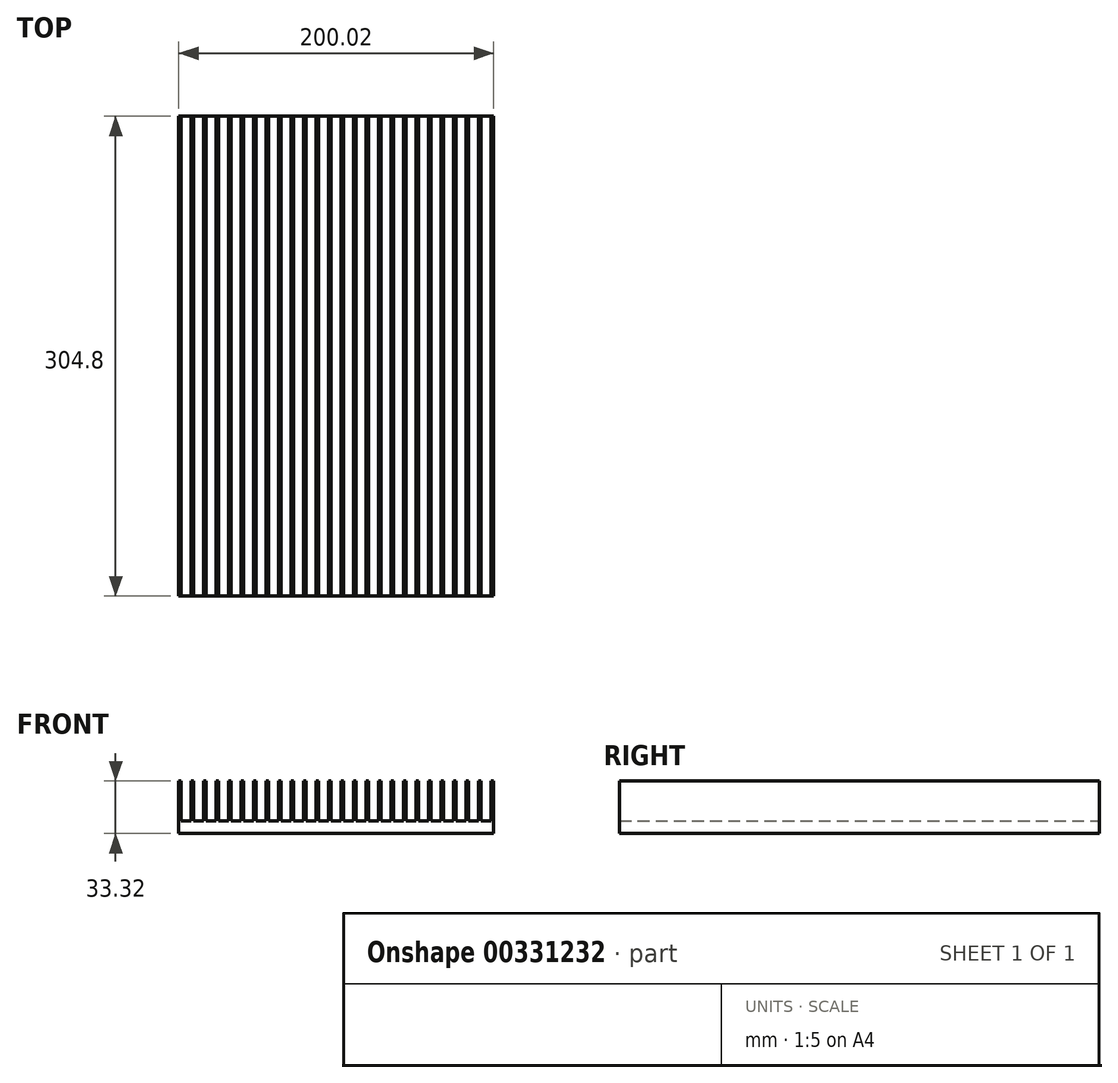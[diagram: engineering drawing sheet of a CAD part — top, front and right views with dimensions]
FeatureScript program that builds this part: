
annotation { "Feature Type Name" : "Feature", "Feature Type Description" : "" }
export const myFeature = defineFeature(function(context is Context, id is Id, definition is map)
    precondition{}
    {
        {
            var Q0;
            Q0=qCreatedBy(makeId("Front.planeOp"),FACE);
            var sketch = newSketch(context, id + "F0", { "sketchPlane" : qUnion([Q0])});
            skLineSegment(sketch, "E0", {"start": v(-100.01, 0) * mm, "end": v(100.01, 0) * mm});
            skLineSegment(sketch, "E1", {"start": v(-100.01, 0) * mm, "end": v(-100.01, 33.32) * mm});
            skLineSegment(sketch, "E2", {"start": v(-100.01, 33.32) * mm, "end": v(-98.49, 33.32) * mm});
            skLineSegment(sketch, "E3", {"start": v(-98.49, 33.32) * mm, "end": v(-98.49, 7.92) * mm});
            skLineSegment(sketch, "E4", {"start": v(-98.49, 7.92) * mm, "end": v(-92.07, 7.92) * mm});
            skLineSegment(sketch, "E5", {"start": v(-92.07, 7.92) * mm, "end": v(-92.07, 33.32) * mm});
            skLineSegment(sketch, "E6", {"start": v(-92.07, 33.32) * mm, "end": v(-90.55, 33.32) * mm});
            skLineSegment(sketch, "E7", {"start": v(-90.55, 33.32) * mm, "end": v(-90.55, 7.92) * mm});
            skLineSegment(sketch, "E8", {"start": v(-90.55, 7.92) * mm, "end": v(-84.13, 7.92) * mm});
            skLineSegment(sketch, "E9", {"start": v(-84.13, 7.92) * mm, "end": v(-84.13, 33.32) * mm});
            skLineSegment(sketch, "E10", {"start": v(-84.13, 33.32) * mm, "end": v(-82.6, 33.32) * mm});
            skLineSegment(sketch, "E11", {"start": v(-82.6, 33.32) * mm, "end": v(-82.6, 7.92) * mm});
            skLineSegment(sketch, "E12", {"start": v(-82.6, 7.92) * mm, "end": v(-76.2, 7.92) * mm});
            skLineSegment(sketch, "E13", {"start": v(-76.2, 7.92) * mm, "end": v(-76.2, 33.32) * mm});
            skLineSegment(sketch, "E14", {"start": v(-76.2, 33.32) * mm, "end": v(-74.67, 33.32) * mm});
            skLineSegment(sketch, "E15", {"start": v(-74.67, 33.32) * mm, "end": v(-74.67, 7.92) * mm});
            skLineSegment(sketch, "E16", {"start": v(-74.67, 7.92) * mm, "end": v(-68.25, 7.92) * mm});
            skLineSegment(sketch, "E17", {"start": v(-68.25, 7.92) * mm, "end": v(-68.25, 33.32) * mm});
            skLineSegment(sketch, "E18", {"start": v(-68.25, 33.32) * mm, "end": v(-66.73, 33.32) * mm});
            skLineSegment(sketch, "E19", {"start": v(-66.73, 33.32) * mm, "end": v(-66.73, 7.92) * mm});
            skLineSegment(sketch, "E20", {"start": v(-66.73, 7.92) * mm, "end": v(-60.31, 7.92) * mm});
            skLineSegment(sketch, "E21", {"start": v(-60.31, 7.92) * mm, "end": v(-60.31, 33.32) * mm});
            skLineSegment(sketch, "E22", {"start": v(-60.31, 33.32) * mm, "end": v(-58.79, 33.32) * mm});
            skLineSegment(sketch, "E23", {"start": v(-58.79, 33.32) * mm, "end": v(-58.79, 7.92) * mm});
            skLineSegment(sketch, "E24", {"start": v(-58.79, 7.92) * mm, "end": v(-52.37, 7.92) * mm});
            skLineSegment(sketch, "E25", {"start": v(-52.37, 7.92) * mm, "end": v(-52.37, 33.32) * mm});
            skLineSegment(sketch, "E26", {"start": v(-52.37, 33.32) * mm, "end": v(-50.85, 33.32) * mm});
            skLineSegment(sketch, "E27", {"start": v(-50.85, 33.32) * mm, "end": v(-50.85, 7.92) * mm});
            skLineSegment(sketch, "E28", {"start": v(-50.85, 7.92) * mm, "end": v(-44.43, 7.92) * mm});
            skLineSegment(sketch, "E29", {"start": v(-44.43, 7.92) * mm, "end": v(-44.43, 33.32) * mm});
            skLineSegment(sketch, "E30", {"start": v(-44.43, 33.32) * mm, "end": v(-42.9, 33.32) * mm});
            skLineSegment(sketch, "E31", {"start": v(-42.9, 33.32) * mm, "end": v(-42.9, 7.92) * mm});
            skLineSegment(sketch, "E32", {"start": v(-42.9, 7.92) * mm, "end": v(-36.5, 7.92) * mm});
            skLineSegment(sketch, "E33", {"start": v(-36.5, 7.92) * mm, "end": v(-36.5, 33.32) * mm});
            skLineSegment(sketch, "E34", {"start": v(-36.5, 33.32) * mm, "end": v(-34.97, 33.32) * mm});
            skLineSegment(sketch, "E35", {"start": v(-34.97, 33.32) * mm, "end": v(-34.97, 7.92) * mm});
            skLineSegment(sketch, "E36", {"start": v(-34.97, 7.92) * mm, "end": v(-28.55, 7.92) * mm});
            skLineSegment(sketch, "E37", {"start": v(-28.55, 7.92) * mm, "end": v(-28.55, 33.32) * mm});
            skLineSegment(sketch, "E38", {"start": v(-28.55, 33.32) * mm, "end": v(-27.03, 33.32) * mm});
            skLineSegment(sketch, "E39", {"start": v(-27.03, 33.32) * mm, "end": v(-27.03, 7.92) * mm});
            skLineSegment(sketch, "E40", {"start": v(-27.03, 7.92) * mm, "end": v(-20.61, 7.92) * mm});
            skLineSegment(sketch, "E41", {"start": v(-20.61, 7.92) * mm, "end": v(-20.61, 33.32) * mm});
            skLineSegment(sketch, "E42", {"start": v(-20.61, 33.32) * mm, "end": v(-19.09, 33.32) * mm});
            skLineSegment(sketch, "E43", {"start": v(-19.09, 33.32) * mm, "end": v(-19.09, 7.92) * mm});
            skLineSegment(sketch, "E44", {"start": v(-19.09, 7.92) * mm, "end": v(-12.67, 7.92) * mm});
            skLineSegment(sketch, "E45", {"start": v(-12.67, 7.92) * mm, "end": v(-12.67, 33.32) * mm});
            skLineSegment(sketch, "E46", {"start": v(-12.67, 33.32) * mm, "end": v(-11.15, 33.32) * mm});
            skLineSegment(sketch, "E47", {"start": v(-11.15, 33.32) * mm, "end": v(-11.15, 7.92) * mm});
            skLineSegment(sketch, "E48", {"start": v(-11.15, 7.92) * mm, "end": v(-4.73, 7.92) * mm});
            skLineSegment(sketch, "E49", {"start": v(-4.73, 7.92) * mm, "end": v(-4.73, 33.32) * mm});
            skLineSegment(sketch, "E50", {"start": v(-4.73, 33.32) * mm, "end": v(-3.2, 33.32) * mm});
            skLineSegment(sketch, "E51", {"start": v(-3.2, 33.32) * mm, "end": v(-3.2, 7.92) * mm});
            skLineSegment(sketch, "E52", {"start": v(-3.2, 7.92) * mm, "end": v(3.2, 7.92) * mm});
            skLineSegment(sketch, "E53", {"start": v(3.2, 7.92) * mm, "end": v(3.2, 33.32) * mm});
            skLineSegment(sketch, "E54", {"start": v(3.2, 33.32) * mm, "end": v(4.73, 33.32) * mm});
            skLineSegment(sketch, "E55", {"start": v(4.73, 33.32) * mm, "end": v(4.73, 7.92) * mm});
            skLineSegment(sketch, "E56", {"start": v(4.73, 7.92) * mm, "end": v(11.15, 7.92) * mm});
            skLineSegment(sketch, "E57", {"start": v(11.15, 7.92) * mm, "end": v(11.15, 33.32) * mm});
            skLineSegment(sketch, "E58", {"start": v(11.15, 33.32) * mm, "end": v(12.67, 33.32) * mm});
            skLineSegment(sketch, "E59", {"start": v(12.67, 33.32) * mm, "end": v(12.67, 7.92) * mm});
            skLineSegment(sketch, "E60", {"start": v(12.67, 7.92) * mm, "end": v(19.09, 7.92) * mm});
            skLineSegment(sketch, "E61", {"start": v(19.09, 7.92) * mm, "end": v(19.09, 33.32) * mm});
            skLineSegment(sketch, "E62", {"start": v(19.09, 33.32) * mm, "end": v(20.61, 33.32) * mm});
            skLineSegment(sketch, "E63", {"start": v(20.61, 33.32) * mm, "end": v(20.61, 7.92) * mm});
            skLineSegment(sketch, "E64", {"start": v(20.61, 7.92) * mm, "end": v(27.03, 7.92) * mm});
            skLineSegment(sketch, "E65", {"start": v(27.03, 7.92) * mm, "end": v(27.03, 33.32) * mm});
            skLineSegment(sketch, "E66", {"start": v(27.03, 33.32) * mm, "end": v(28.55, 33.32) * mm});
            skLineSegment(sketch, "E67", {"start": v(28.55, 33.32) * mm, "end": v(28.55, 7.92) * mm});
            skLineSegment(sketch, "E68", {"start": v(28.55, 7.92) * mm, "end": v(34.97, 7.92) * mm});
            skLineSegment(sketch, "E69", {"start": v(34.97, 7.92) * mm, "end": v(34.97, 33.32) * mm});
            skLineSegment(sketch, "E70", {"start": v(34.97, 33.32) * mm, "end": v(36.5, 33.32) * mm});
            skLineSegment(sketch, "E71", {"start": v(36.5, 33.32) * mm, "end": v(36.5, 7.92) * mm});
            skLineSegment(sketch, "E72", {"start": v(36.5, 7.92) * mm, "end": v(42.9, 7.92) * mm});
            skLineSegment(sketch, "E73", {"start": v(42.9, 7.92) * mm, "end": v(42.9, 33.32) * mm});
            skLineSegment(sketch, "E74", {"start": v(42.9, 33.32) * mm, "end": v(44.43, 33.32) * mm});
            skLineSegment(sketch, "E75", {"start": v(44.43, 33.32) * mm, "end": v(44.43, 7.92) * mm});
            skLineSegment(sketch, "E76", {"start": v(44.43, 7.92) * mm, "end": v(50.85, 7.92) * mm});
            skLineSegment(sketch, "E77", {"start": v(50.85, 7.92) * mm, "end": v(50.85, 33.32) * mm});
            skLineSegment(sketch, "E78", {"start": v(50.85, 33.32) * mm, "end": v(52.37, 33.32) * mm});
            skLineSegment(sketch, "E79", {"start": v(52.37, 33.32) * mm, "end": v(52.37, 7.92) * mm});
            skLineSegment(sketch, "E80", {"start": v(52.37, 7.92) * mm, "end": v(58.79, 7.92) * mm});
            skLineSegment(sketch, "E81", {"start": v(58.79, 7.92) * mm, "end": v(58.79, 33.32) * mm});
            skLineSegment(sketch, "E82", {"start": v(58.79, 33.32) * mm, "end": v(60.31, 33.32) * mm});
            skLineSegment(sketch, "E83", {"start": v(60.31, 33.32) * mm, "end": v(60.31, 7.92) * mm});
            skLineSegment(sketch, "E84", {"start": v(60.31, 7.92) * mm, "end": v(66.73, 7.92) * mm});
            skLineSegment(sketch, "E85", {"start": v(66.73, 7.92) * mm, "end": v(66.73, 33.32) * mm});
            skLineSegment(sketch, "E86", {"start": v(66.73, 33.32) * mm, "end": v(68.25, 33.32) * mm});
            skLineSegment(sketch, "E87", {"start": v(68.25, 33.32) * mm, "end": v(68.25, 7.92) * mm});
            skLineSegment(sketch, "E88", {"start": v(68.25, 7.92) * mm, "end": v(74.67, 7.92) * mm});
            skLineSegment(sketch, "E89", {"start": v(74.67, 7.92) * mm, "end": v(74.67, 33.32) * mm});
            skLineSegment(sketch, "E90", {"start": v(74.67, 33.32) * mm, "end": v(76.2, 33.32) * mm});
            skLineSegment(sketch, "E91", {"start": v(76.2, 33.32) * mm, "end": v(76.2, 7.92) * mm});
            skLineSegment(sketch, "E92", {"start": v(76.2, 7.92) * mm, "end": v(82.6, 7.92) * mm});
            skLineSegment(sketch, "E93", {"start": v(82.6, 7.92) * mm, "end": v(82.6, 33.32) * mm});
            skLineSegment(sketch, "E94", {"start": v(82.6, 33.32) * mm, "end": v(84.13, 33.32) * mm});
            skLineSegment(sketch, "E95", {"start": v(84.13, 33.32) * mm, "end": v(84.13, 7.92) * mm});
            skLineSegment(sketch, "E96", {"start": v(84.13, 7.92) * mm, "end": v(90.55, 7.92) * mm});
            skLineSegment(sketch, "E97", {"start": v(90.55, 7.92) * mm, "end": v(90.55, 33.32) * mm});
            skLineSegment(sketch, "E98", {"start": v(90.55, 33.32) * mm, "end": v(92.07, 33.32) * mm});
            skLineSegment(sketch, "E99", {"start": v(92.07, 33.32) * mm, "end": v(92.07, 7.92) * mm});
            skLineSegment(sketch, "E100", {"start": v(92.07, 7.92) * mm, "end": v(98.49, 7.92) * mm});
            skLineSegment(sketch, "E101", {"start": v(98.49, 7.92) * mm, "end": v(98.49, 33.32) * mm});
            skLineSegment(sketch, "E102", {"start": v(98.49, 33.32) * mm, "end": v(100.01, 33.32) * mm});
            skLineSegment(sketch, "E103", {"start": v(100.01, 33.32) * mm, "end": v(100.01, 0) * mm});
            skSolve(sketch);
        }
        {
            var Q0;
            Q0 = qSketchRegion(id + "F0", true);
            extrude(context, id + "F1", {"entities" : qUnion([Q0]), "depth" : 304.8 * mm});
        }
    });
